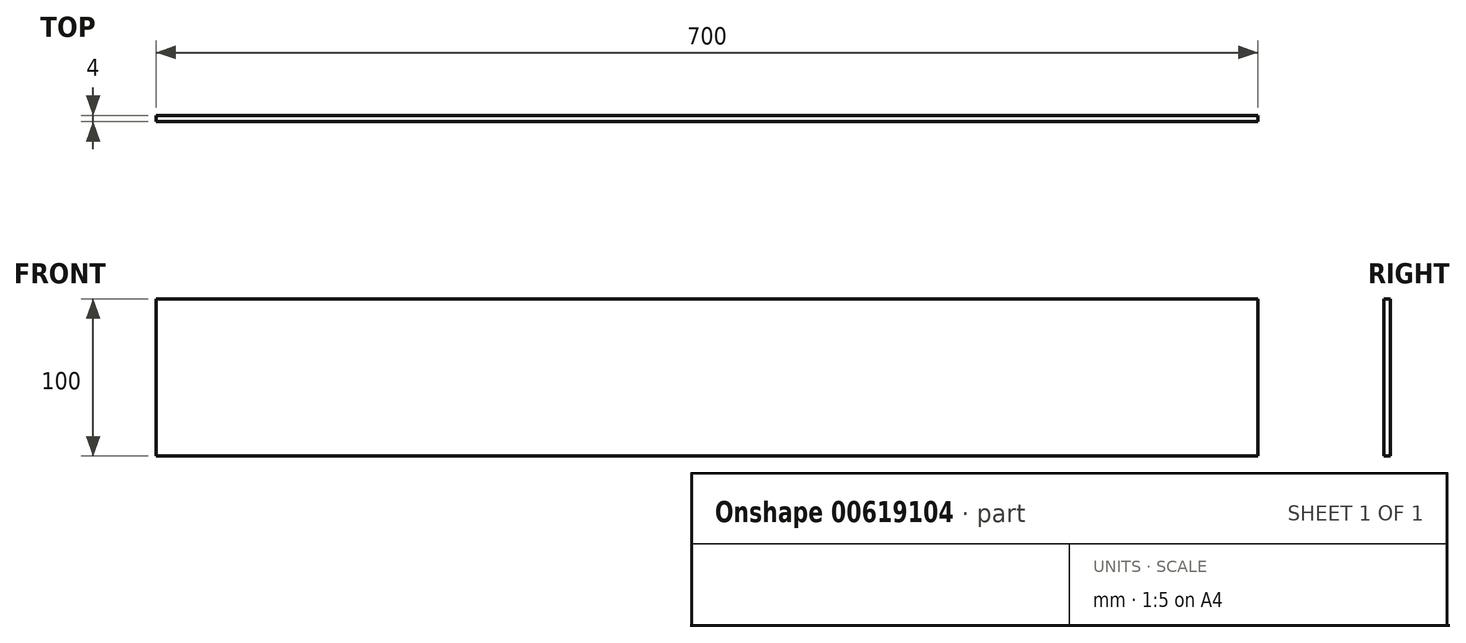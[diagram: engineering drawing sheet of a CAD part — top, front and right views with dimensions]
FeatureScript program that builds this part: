
annotation { "Feature Type Name" : "Feature", "Feature Type Description" : "" }
export const myFeature = defineFeature(function(context is Context, id is Id, definition is map)
    precondition{}
    {
        {
            var Q0;
            Q0=qCreatedBy(makeId("Front.planeOp"),FACE);
            var sketch = newSketch(context, id + "F0", { "sketchPlane" : qUnion([Q0])});
            skLineSegment(sketch, "E0.bottom", {"start": v(629.47, 0) * mm, "end": v(-70.53, 0) * mm});
            skLineSegment(sketch, "E0.top", {"start": v(629.47, 100) * mm, "end": v(-70.53, 100) * mm});
            skLineSegment(sketch, "E0.left", {"start": v(629.47, 0) * mm, "end": v(629.47, 100) * mm});
            skLineSegment(sketch, "E0.right", {"start": v(-70.53, 0) * mm, "end": v(-70.53, 100) * mm});
            skSolve(sketch);
        }
        {
            var Q0;
            Q0=qSketchRegion(id+"F0",true);
            extrude(context, id + "F1", {"entities" : qUnion([Q0]), "depth" : 4 * mm, "offsetDistance" : 25 * mm});
        }
    });
